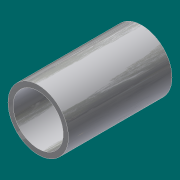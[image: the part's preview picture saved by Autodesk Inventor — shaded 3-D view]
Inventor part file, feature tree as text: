
AUTODESK INVENTOR PART (.ipt)
format: ipt  version: 2017 (Build 210142000, 142)  size: 93,696 bytes
history: native  units: in
note: dims shown in document units (in); Inventor stores cm internally (conversion verified against a paired STEP export)
features: extrude x1, sketch x1
ambient origin geometry x8: Origin, YZ Plane, XZ Plane, XY Plane, X Axis, Y Axis, Z Axis, Center Point
bodies: Solid1 (feature_tree)
feature tree (2):
  extrude  "Extrusion1"  Depth=6.0in
  sketch  "Sketch1"  dims[d0=3.5in d1=2.9in d2=6.0in d3=0.0in]
